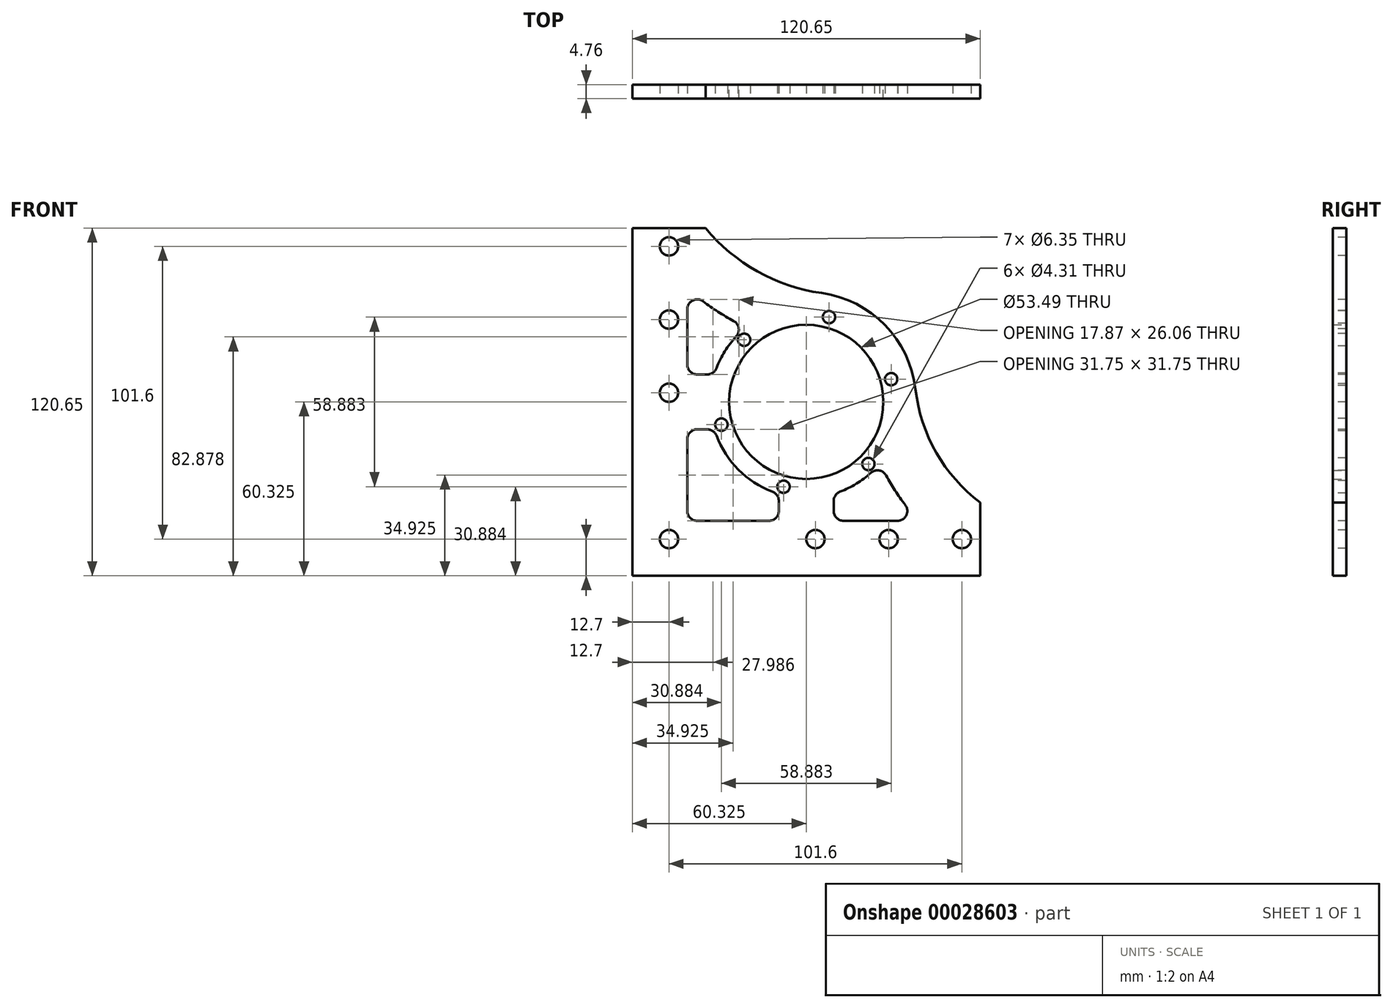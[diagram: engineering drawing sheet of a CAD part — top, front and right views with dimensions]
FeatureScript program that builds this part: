
annotation { "Feature Type Name" : "Feature", "Feature Type Description" : "" }
export const myFeature = defineFeature(function(context is Context, id is Id, definition is map)
    precondition{}
    {
        {
            var Q0;
            Q0=qCreatedBy(makeId("Front.planeOp"),FACE);
            var sketch = newSketch(context, id + "F0", { "sketchPlane" : qUnion([Q0])});
            skLineSegment(sketch, "E0.bottom", {"start": v(0, 0) * mm, "end": v(120.65, 0) * mm});
            skLineSegment(sketch, "E0.top", {"start": v(0, 120.65) * mm, "end": v(25.4, 120.65) * mm});
            skLineSegment(sketch, "E0.left", {"start": v(0, 0) * mm, "end": v(0, 120.65) * mm});
            skLineSegment(sketch, "E0.right", {"start": v(120.65, 0) * mm, "end": v(120.65, 25.4) * mm});
            skCircle(sketch, "E1", {"center": v(60.33, 60.32) * mm, "radius": 26.75 * mm});
            skArc(sketch, "E2", {"start": v(25.4, 120.65) * mm, "mid": v(43.4, 105.6) * mm, "end": v(65.62, 98.11) * mm});
            skArc(sketch, "E3.trimOffspring", {"start": v(98.24, 64.65) * mm, "mid": v(105.41, 42.72) * mm, "end": v(120.65, 25.4) * mm});
            skLineSegment(sketch, "E4", {"start": v(60.33, 60.33) * mm, "end": v(-72.5, 60.33) * mm, "construction": true});
            skLineSegment(sketch, "E5", {"start": v(60.32, 60.32) * mm, "end": v(60.32, -10.58) * mm, "construction": true});
            skArc(sketch, "E6.trimOffspring", {"start": v(98.24, 64.65) * mm, "mid": v(87.65, 86.96) * mm, "end": v(65.62, 98.11) * mm});
            skSolve(sketch);
        }
        {
            var Q0;
            Q0=makeQuery(id+"F0.imprint","IMPRINT",FACE,{"disambiguationData":[TD([[makeQuery(id+"F0.imprint","IMPRINT",EDGE,{"derivedFrom":sQuery(id+"F0.wireOp",EDGE,"E0.bottom")}),1.0]])]});
            extrude(context, id + "F1", {"entities" : qUnion([Q0]), "depth" : 4.76 * mm});
        }
        {
            var Q0;
            Q0=makeQuery(id+"F1.opExtrude","CAP_FACE",FACE,{"disambiguationData":[OSD([sQuery(id+"F0.wireOp",EDGE,"E0.bottom"),sQuery(id+"F0.wireOp",EDGE,"E0.top"),sQuery(id+"F0.wireOp",EDGE,"E0.left"),sQuery(id+"F0.wireOp",EDGE,"E0.right"),sQuery(id+"F0.wireOp",EDGE,"E1"),sQuery(id+"F0.wireOp",EDGE,"E2"),sQuery(id+"F0.wireOp",EDGE,"E3.trimOffspring"),sQuery(id+"F0.wireOp",EDGE,"E6.trimOffspring")])],"isStart":false});
            var sketch = newSketch(context, id + "F2", { "sketchPlane" : qUnion([Q0])});
            skCircle(sketch, "E7", {"center": v(60.33, 60.32) * mm, "radius": 33.28 * mm});
            skLineSegment(sketch, "E8", {"start": v(19.05, 99.78) * mm, "end": v(19.05, 69.85) * mm});
            skLineSegment(sketch, "E9", {"start": v(19.05, 69.85) * mm, "end": v(28.44, 69.85) * mm});
            skLineSegment(sketch, "E10", {"start": v(19.05, 50.8) * mm, "end": v(19.05, 19.05) * mm});
            skLineSegment(sketch, "E11", {"start": v(19.05, 19.05) * mm, "end": v(50.8, 19.05) * mm});
            skLineSegment(sketch, "E12", {"start": v(50.8, 19.05) * mm, "end": v(50.8, 28.44) * mm});
            skLineSegment(sketch, "E13", {"start": v(69.85, 19.05) * mm, "end": v(99.34, 19.05) * mm});
            skLineSegment(sketch, "E14", {"start": v(69.85, 28.44) * mm, "end": v(69.85, 19.05) * mm});
            skLineSegment(sketch, "E15", {"start": v(28.44, 50.8) * mm, "end": v(19.05, 50.8) * mm});
            skArc(sketch, "E16.0", {"start": v(85.9, 39.03) * mm, "mid": v(91.83, 28.5) * mm, "end": v(99.34, 19.05) * mm});
            skArc(sketch, "E17.0", {"start": v(19.05, 99.78) * mm, "mid": v(28.74, 92.25) * mm, "end": v(39.44, 86.23) * mm});
            skSolve(sketch);
        }
        {
            var Q0;
            Q0=makeQuery(id+"F2.imprint","IMPRINT",FACE,{"disambiguationData":[TD([[makeQuery(id+"F2.imprint","IMPRINT",EDGE,{"derivedFrom":sQuery(id+"F2.wireOp",EDGE,"E8")}),1.0]])]});
            var Q1;
            Q1=makeQuery(id+"F2.imprint","IMPRINT",FACE,{"disambiguationData":[TD([[makeQuery(id+"F2.imprint","IMPRINT",EDGE,{"derivedFrom":sQuery(id+"F2.wireOp",EDGE,"E10")}),1.0]])]});
            var Q2;
            Q2=makeQuery(id+"F2.imprint","IMPRINT",FACE,{"disambiguationData":[TD([[makeQuery(id+"F2.imprint","IMPRINT",EDGE,{"derivedFrom":sQuery(id+"F2.wireOp",EDGE,"E13")}),1.0]])]});
            extrude(context, id + "F3", {"entities" : qUnion([Q0, Q1, Q2]), "operationType" : NewBodyOperationType.REMOVE, "endBound" : BoundingType.THROUGH_ALL, "oppositeDirection" : true, "depth" : 25.4 * mm});
        }
        {
            var Q0;
            Q0=makeQuery(id+"F3.boolean.opBoolean","COPY",EDGE,{"derivedFrom":makeQuery(id+"F3.opExtrude","SWEPT_EDGE",EDGE,{"disambiguationData":[OSD([sQuery(id+"F2.wireOp",EDGE,"E8"),sQuery(id+"F2.wireOp",EDGE,"E9")])]})});
            var Q1;
            Q1=makeQuery(id+"F3.boolean.opBoolean","COPY",EDGE,{"derivedFrom":makeQuery(id+"F3.opExtrude","SWEPT_EDGE",EDGE,{"disambiguationData":[OSD([sQuery(id+"F2.wireOp",EDGE,"E7"),sQuery(id+"F2.wireOp",EDGE,"E17.0")])]})});
            var Q2;
            Q2=makeQuery(id+"F3.boolean.opBoolean","COPY",EDGE,{"derivedFrom":makeQuery(id+"F3.opExtrude","SWEPT_EDGE",EDGE,{"disambiguationData":[OSD([sQuery(id+"F2.wireOp",EDGE,"E8"),sQuery(id+"F2.wireOp",EDGE,"E17.0")])]})});
            var Q3;
            Q3=makeQuery(id+"F3.boolean.opBoolean","COPY",EDGE,{"derivedFrom":makeQuery(id+"F3.opExtrude","SWEPT_EDGE",EDGE,{"disambiguationData":[OSD([sQuery(id+"F2.wireOp",EDGE,"E10"),sQuery(id+"F2.wireOp",EDGE,"E15")])]})});
            var Q4;
            Q4=makeQuery(id+"F3.boolean.opBoolean","COPY",EDGE,{"derivedFrom":makeQuery(id+"F3.opExtrude","SWEPT_EDGE",EDGE,{"disambiguationData":[OSD([sQuery(id+"F2.wireOp",EDGE,"E7"),sQuery(id+"F2.wireOp",EDGE,"E15")])]})});
            var Q5;
            Q5=makeQuery(id+"F3.boolean.opBoolean","COPY",EDGE,{"derivedFrom":makeQuery(id+"F3.opExtrude","SWEPT_EDGE",EDGE,{"disambiguationData":[OSD([sQuery(id+"F2.wireOp",EDGE,"E7"),sQuery(id+"F2.wireOp",EDGE,"E12")])]})});
            var Q6;
            Q6=makeQuery(id+"F3.boolean.opBoolean","COPY",EDGE,{"derivedFrom":makeQuery(id+"F3.opExtrude","SWEPT_EDGE",EDGE,{"disambiguationData":[OSD([sQuery(id+"F2.wireOp",EDGE,"E11"),sQuery(id+"F2.wireOp",EDGE,"E12")])]})});
            var Q7;
            Q7=makeQuery(id+"F3.boolean.opBoolean","COPY",EDGE,{"derivedFrom":makeQuery(id+"F3.opExtrude","SWEPT_EDGE",EDGE,{"disambiguationData":[OSD([sQuery(id+"F2.wireOp",EDGE,"E10"),sQuery(id+"F2.wireOp",EDGE,"E11")])]})});
            var Q8;
            Q8=makeQuery(id+"F3.boolean.opBoolean","COPY",EDGE,{"derivedFrom":makeQuery(id+"F3.opExtrude","SWEPT_EDGE",EDGE,{"disambiguationData":[OSD([sQuery(id+"F2.wireOp",EDGE,"E13"),sQuery(id+"F2.wireOp",EDGE,"E16.0")])]})});
            var Q9;
            Q9=makeQuery(id+"F3.boolean.opBoolean","COPY",EDGE,{"derivedFrom":makeQuery(id+"F3.opExtrude","SWEPT_EDGE",EDGE,{"disambiguationData":[OSD([sQuery(id+"F2.wireOp",EDGE,"E7"),sQuery(id+"F2.wireOp",EDGE,"E14")])]})});
            var Q10;
            Q10=makeQuery(id+"F3.boolean.opBoolean","COPY",EDGE,{"derivedFrom":makeQuery(id+"F3.opExtrude","SWEPT_EDGE",EDGE,{"disambiguationData":[OSD([sQuery(id+"F2.wireOp",EDGE,"E7"),sQuery(id+"F2.wireOp",EDGE,"E16.0")])]})});
            var Q11;
            Q11=makeQuery(id+"F3.boolean.opBoolean","COPY",EDGE,{"derivedFrom":makeQuery(id+"F3.opExtrude","SWEPT_EDGE",EDGE,{"disambiguationData":[OSD([sQuery(id+"F2.wireOp",EDGE,"E13"),sQuery(id+"F2.wireOp",EDGE,"E14")])]})});
            var Q12;
            Q12=makeQuery(id+"F3.boolean.opBoolean","COPY",EDGE,{"derivedFrom":makeQuery(id+"F3.opExtrude","SWEPT_EDGE",EDGE,{"disambiguationData":[OSD([sQuery(id+"F2.wireOp",EDGE,"E7"),sQuery(id+"F2.wireOp",EDGE,"E9")])]})});
            fillet(context, id + "F4", {"entities" : qUnion([Q0, Q1, Q2, Q3, Q4, Q5, Q6, Q7, Q8, Q9, Q10, Q11, Q12]), "radius" : 3.43 * mm, "tangentPropagation" : true, "allowEdgeOverflow" : false});
        }
        {
            var Q0;
            Q0=makeQuery(id+"F1.opExtrude","CAP_FACE",FACE,{"disambiguationData":[OSD([sQuery(id+"F0.wireOp",EDGE,"E0.bottom"),sQuery(id+"F0.wireOp",EDGE,"E0.top"),sQuery(id+"F0.wireOp",EDGE,"E0.left"),sQuery(id+"F0.wireOp",EDGE,"E0.right"),sQuery(id+"F0.wireOp",EDGE,"E1"),sQuery(id+"F0.wireOp",EDGE,"E2"),sQuery(id+"F0.wireOp",EDGE,"E3.trimOffspring"),sQuery(id+"F0.wireOp",EDGE,"E6.trimOffspring")])],"isStart":false});
            var sketch = newSketch(context, id + "F5", { "sketchPlane" : qUnion([Q0])});
            skLineSegment(sketch, "E18", {"start": v(12.7, 114.3) * mm, "end": v(12.7, 12.7) * mm, "construction": true});
            skLineSegment(sketch, "E19", {"start": v(12.7, 12.7) * mm, "end": v(114.3, 12.7) * mm, "construction": true});
            skPoint(sketch, "E20", {"position": v(12.7, 88.9) * mm});
            skPoint(sketch, "E21", {"position": v(12.7, 63.5) * mm});
            skPoint(sketch, "E22", {"position": v(88.9, 12.7) * mm});
            skPoint(sketch, "E23", {"position": v(63.5, 12.7) * mm});
            skCircle(sketch, "E24.cCircle", {"center": v(60.33, 60.32) * mm, "radius": 30.48 * mm, "construction": true});
            skLineSegment(sketch, "E24.0", {"start": v(38.77, 81.88) * mm, "end": v(68.21, 89.77) * mm});
            skLineSegment(sketch, "E24.1", {"start": v(68.21, 89.77) * mm, "end": v(89.77, 68.21) * mm});
            skLineSegment(sketch, "E24.2", {"start": v(89.77, 68.21) * mm, "end": v(81.88, 38.77) * mm});
            skLineSegment(sketch, "E24.3", {"start": v(81.88, 38.77) * mm, "end": v(52.44, 30.88) * mm});
            skLineSegment(sketch, "E24.4", {"start": v(52.44, 30.88) * mm, "end": v(30.88, 52.44) * mm});
            skLineSegment(sketch, "E24.5", {"start": v(30.88, 52.44) * mm, "end": v(38.77, 81.88) * mm});
            skLineSegment(sketch, "E25", {"start": v(60.33, 60.32) * mm, "end": v(96.86, 96.86) * mm, "construction": true});
            skSolve(sketch);
        }
        {
            var Q0;
            Q0=sQuery(id+"F5.wireOp",VERTEX,"E24.0.start");
            var Q1;
            Q1=sQuery(id+"F5.wireOp",VERTEX,"E24.1.start");
            var Q2;
            Q2=sQuery(id+"F5.wireOp",VERTEX,"E24.2.start");
            var Q3;
            Q3=sQuery(id+"F5.wireOp",VERTEX,"E24.3.start");
            var Q4;
            Q4=sQuery(id+"F5.wireOp",VERTEX,"E24.4.start");
            var Q5;
            Q5=sQuery(id+"F5.wireOp",VERTEX,"E24.5.start");
            var Q6;
            Q6=makeQuery(id+"F1.opExtrude","SWEPT_BODY",BODY,{"disambiguationData":[OSD([sQuery(id+"F0.wireOp",EDGE,"E0.bottom"),sQuery(id+"F0.wireOp",EDGE,"E0.top"),sQuery(id+"F0.wireOp",EDGE,"E0.left"),sQuery(id+"F0.wireOp",EDGE,"E0.right"),sQuery(id+"F0.wireOp",EDGE,"E1"),sQuery(id+"F0.wireOp",EDGE,"E2"),sQuery(id+"F0.wireOp",EDGE,"E3.trimOffspring"),sQuery(id+"F0.wireOp",EDGE,"E6.trimOffspring")])]});
            hole(context, id + "F6", {"style" : HoleStyle.SIMPLE, "holeDiameter" : 4.3 * mm, "endStyle" : HoleEndStyle.THROUGH, "locations" : qUnion([Q0, Q1, Q2, Q3, Q4, Q5]), "scope" : qUnion([Q6])});
        }
        {
            var Q0;
            Q0=sQuery(id+"F5.wireOp",VERTEX,"E18.start");
            var Q1;
            Q1=sQuery(id+"F5.wireOp",VERTEX,"E20");
            var Q2;
            Q2=sQuery(id+"F5.wireOp",VERTEX,"E21");
            var Q3;
            Q3=sQuery(id+"F5.wireOp",VERTEX,"E19.start");
            var Q4;
            Q4=sQuery(id+"F5.wireOp",VERTEX,"E23");
            var Q5;
            Q5=sQuery(id+"F5.wireOp",VERTEX,"E22");
            var Q6;
            Q6=sQuery(id+"F5.wireOp",VERTEX,"E19.end");
            var Q7;
            Q7=makeQuery(id+"F1.opExtrude","SWEPT_BODY",BODY,{"disambiguationData":[OSD([sQuery(id+"F0.wireOp",EDGE,"E0.bottom"),sQuery(id+"F0.wireOp",EDGE,"E0.top"),sQuery(id+"F0.wireOp",EDGE,"E0.left"),sQuery(id+"F0.wireOp",EDGE,"E0.right"),sQuery(id+"F0.wireOp",EDGE,"E1"),sQuery(id+"F0.wireOp",EDGE,"E2"),sQuery(id+"F0.wireOp",EDGE,"E3.trimOffspring"),sQuery(id+"F0.wireOp",EDGE,"E6.trimOffspring")])]});
            hole(context, id + "F7", {"style" : HoleStyle.SIMPLE, "holeDiameter" : 6.35 * mm, "endStyle" : HoleEndStyle.THROUGH, "locations" : qUnion([Q0, Q1, Q2, Q3, Q4, Q5, Q6]), "scope" : qUnion([Q7])});
        }
    });
